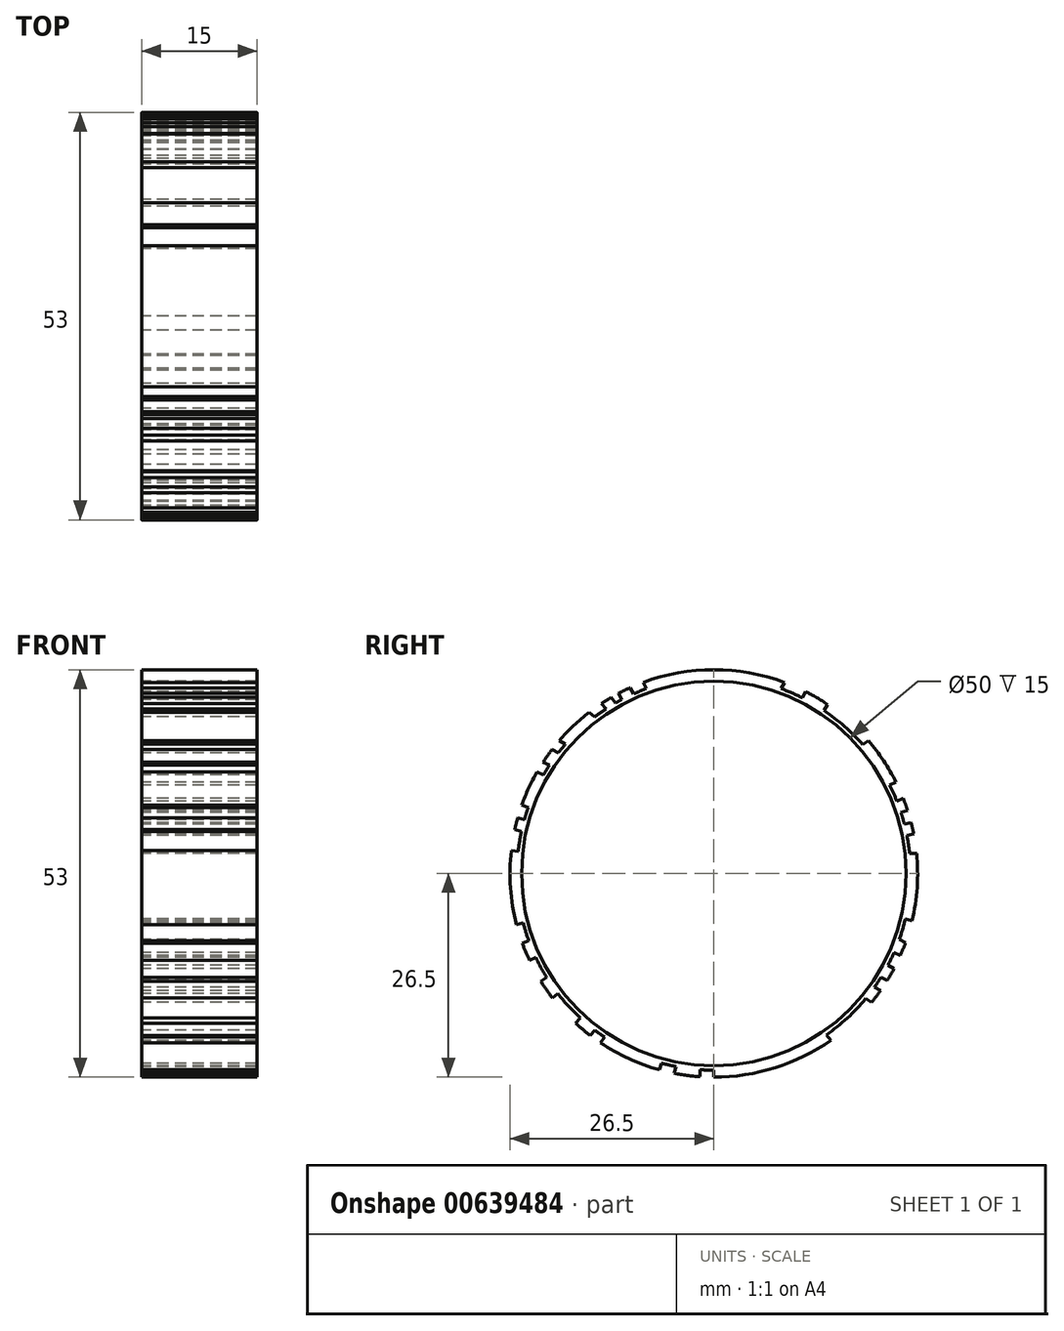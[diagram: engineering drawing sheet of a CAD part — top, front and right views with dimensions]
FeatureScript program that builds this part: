
annotation { "Feature Type Name" : "Feature", "Feature Type Description" : "" }
export const myFeature = defineFeature(function(context is Context, id is Id, definition is map)
    precondition{}
    {
        {
            var Q0;
            Q0=qCreatedBy(makeId("Right.planeOp"),FACE);
            var sketch = newSketch(context, id + "F0", { "sketchPlane" : qUnion([Q0])});
            skCircle(sketch, "E0", {"center": v(0, 0) * mm, "radius": 25 * mm});
            skSolve(sketch);
        }
        {
            var Q0;
            Q0=makeQuery(id+"F0.imprint","IMPRINT",FACE,{"disambiguationData":[TD([[makeQuery(id+"F0.imprint","IMPRINT",EDGE,{"derivedFrom":sQuery(id+"F0.wireOp",EDGE,"E0")}),1.0]])]});
            extrude(context, id + "F1", {"entities" : qUnion([Q0]), "depth" : 15 * mm, "offsetDistance" : 25 * mm});
        }
        {
            var Q0;
            Q0=qCreatedBy(makeId("Right.planeOp"),FACE);
            var sketch = newSketch(context, id + "F2", { "sketchPlane" : qUnion([Q0])});
            skArc(sketch, "E1", {"start": v(9.17, 24.86) * mm, "mid": v(0, 26.5) * mm, "end": v(-9.17, 24.86) * mm});
            skArc(sketch, "E2.0", {"start": v(-15.02, 19.99) * mm, "mid": v(13.77, -20.87) * mm, "end": v(-12.47, 21.67) * mm});
            skLineSegment(sketch, "E3", {"start": v(8.77, 24.05) * mm, "end": v(9.17, 24.86) * mm});
            skLineSegment(sketch, "E4.MirrorCS", {"start": v(-8.77, 24.05) * mm, "end": v(-9.17, 24.86) * mm});
            skLineSegment(sketch, "E5.0", {"start": v(11.2, 22.2) * mm, "end": v(11.26, 22.32) * mm});
            skLineSegment(sketch, "E6", {"start": v(14.32, 21.21) * mm, "end": v(14.77, 22) * mm});
            skLineSegment(sketch, "E7", {"start": v(11.86, 23.55) * mm, "end": v(11.92, 23.67) * mm});
            skLineSegment(sketch, "E8", {"start": v(-10.45, 23.36) * mm, "end": v(-10.88, 24.16) * mm});
            skLineSegment(sketch, "E9", {"start": v(-11.96, 22.63) * mm, "end": v(-12.4, 23.42) * mm});
            skArc(sketch, "E10.trimOffspring", {"start": v(-10.88, 24.16) * mm, "mid": v(-11.65, 23.8) * mm, "end": v(-12.4, 23.42) * mm});
            skLineSegment(sketch, "E11", {"start": v(19.35, 16.75) * mm, "end": v(20.1, 17.27) * mm});
            skLineSegment(sketch, "E12", {"start": v(22.88, 11.47) * mm, "end": v(23.7, 11.85) * mm});
            skLineSegment(sketch, "E13", {"start": v(23.8, 9.42) * mm, "end": v(24.64, 9.76) * mm});
            skLineSegment(sketch, "E14", {"start": v(24.33, 7.95) * mm, "end": v(25.2, 8.22) * mm});
            skArc(sketch, "E15.trimOffspring", {"start": v(23.7, 11.85) * mm, "mid": v(22.07, 14.67) * mm, "end": v(20.1, 17.27) * mm});
            skArc(sketch, "E16.trimOffspring", {"start": v(14.77, 22) * mm, "mid": v(13.37, 22.88) * mm, "end": v(11.92, 23.67) * mm});
            skLineSegment(sketch, "E17", {"start": v(24.78, 6.4) * mm, "end": v(25.66, 6.62) * mm});
            skLineSegment(sketch, "E18", {"start": v(25.1, 4.95) * mm, "end": v(26, 5.12) * mm});
            skArc(sketch, "E19.trimOffspring", {"start": v(25.2, 8.22) * mm, "mid": v(24.93, 9) * mm, "end": v(24.64, 9.76) * mm});
            skLineSegment(sketch, "E20", {"start": v(25.46, 2.62) * mm, "end": v(26.37, 2.62) * mm});
            skLineSegment(sketch, "E21", {"start": v(24.9, -5.88) * mm, "end": v(25.77, -6.18) * mm});
            skArc(sketch, "E22.trimOffspring", {"start": v(26, 5.12) * mm, "mid": v(25.84, 5.88) * mm, "end": v(25.66, 6.62) * mm});
            skLineSegment(sketch, "E23", {"start": v(-12.8, 22.16) * mm, "end": v(-13.32, 22.9) * mm});
            skLineSegment(sketch, "E24", {"start": v(-14.02, 21.41) * mm, "end": v(-14.6, 22.11) * mm});
            skArc(sketch, "E25.trimOffspring", {"start": v(-13.32, 22.9) * mm, "mid": v(-13.97, 22.52) * mm, "end": v(-14.6, 22.11) * mm});
            skLineSegment(sketch, "E26", {"start": v(-15.49, 20.38) * mm, "end": v(-16.2, 20.97) * mm});
            skLineSegment(sketch, "E27", {"start": v(-19.3, 16.8) * mm, "end": v(-20.08, 17.29) * mm});
            skArc(sketch, "E28.trimOffspring", {"start": v(-16.2, 20.97) * mm, "mid": v(-18.24, 19.23) * mm, "end": v(-20.08, 17.29) * mm});
            skLineSegment(sketch, "E29", {"start": v(-12.52, 21.75) * mm, "end": v(-12.47, 21.67) * mm});
            skLineSegment(sketch, "E30", {"start": v(24.12, -8.56) * mm, "end": v(24.93, -9) * mm});
            skLineSegment(sketch, "E31", {"start": v(23.44, -10.28) * mm, "end": v(24.27, -10.65) * mm});
            skArc(sketch, "E32.trimOffspring", {"start": v(25.77, -6.18) * mm, "mid": v(26.44, -1.8) * mm, "end": v(26.37, 2.62) * mm});
            skLineSegment(sketch, "E33", {"start": v(22.64, -11.94) * mm, "end": v(23.43, -12.38) * mm});
            skLineSegment(sketch, "E34", {"start": v(21.75, -13.5) * mm, "end": v(22.56, -13.9) * mm});
            skArc(sketch, "E35.trimOffspring", {"start": v(24.27, -10.65) * mm, "mid": v(24.61, -9.83) * mm, "end": v(24.93, -9) * mm});
            skLineSegment(sketch, "E36", {"start": v(20.9, -14.77) * mm, "end": v(21.67, -15.25) * mm});
            skLineSegment(sketch, "E37", {"start": v(19.75, -16.27) * mm, "end": v(20.52, -16.77) * mm});
            skArc(sketch, "E38.trimOffspring", {"start": v(22.56, -13.9) * mm, "mid": v(23, -13.15) * mm, "end": v(23.43, -12.38) * mm});
            skLineSegment(sketch, "E39", {"start": v(14.63, -21) * mm, "end": v(15.22, -21.7) * mm});
            skLineSegment(sketch, "E40", {"start": v(0, -25.6) * mm, "end": v(0, -26.5) * mm});
            skArc(sketch, "E41.trimOffspring", {"start": v(20.52, -16.77) * mm, "mid": v(21.1, -16.02) * mm, "end": v(21.67, -15.25) * mm});
            skLineSegment(sketch, "E42", {"start": v(-1.81, -25.53) * mm, "end": v(-1.81, -26.44) * mm});
            skLineSegment(sketch, "E43", {"start": v(-4.92, -25.12) * mm, "end": v(-5.14, -26) * mm});
            skArc(sketch, "E44.trimOffspring", {"start": v(0, -26.5) * mm, "mid": v(7.98, -25.27) * mm, "end": v(15.22, -21.7) * mm});
            skLineSegment(sketch, "E45", {"start": v(-20.23, 15.68) * mm, "end": v(-21.01, 16.14) * mm});
            skLineSegment(sketch, "E46", {"start": v(-21.37, 14.08) * mm, "end": v(-22.2, 14.46) * mm});
            skArc(sketch, "E47.trimOffspring", {"start": v(-21.01, 16.14) * mm, "mid": v(-21.63, 15.31) * mm, "end": v(-22.2, 14.46) * mm});
            skLineSegment(sketch, "E48", {"start": v(-22.15, 12.81) * mm, "end": v(-22.98, 13.2) * mm});
            skLineSegment(sketch, "E49", {"start": v(-24.1, 8.6) * mm, "end": v(-24.96, 8.91) * mm});
            skArc(sketch, "E50.trimOffspring", {"start": v(-22.98, 13.2) * mm, "mid": v(-24.06, 11.1) * mm, "end": v(-24.96, 8.91) * mm});
            skLineSegment(sketch, "E51", {"start": v(-6.8, -24.68) * mm, "end": v(-7.05, -25.55) * mm});
            skLineSegment(sketch, "E52", {"start": v(-14.2, -21.3) * mm, "end": v(-14.76, -22) * mm});
            skArc(sketch, "E53.trimOffspring", {"start": v(-5.14, -26) * mm, "mid": v(-3.49, -26.27) * mm, "end": v(-1.81, -26.44) * mm});
            skLineSegment(sketch, "E54", {"start": v(-24.62, 7) * mm, "end": v(-25.49, 7.26) * mm});
            skLineSegment(sketch, "E55", {"start": v(-25, 5.46) * mm, "end": v(-25.88, 5.7) * mm});
            skArc(sketch, "E56.trimOffspring", {"start": v(-25.49, 7.26) * mm, "mid": v(-25.7, 6.48) * mm, "end": v(-25.88, 5.7) * mm});
            skLineSegment(sketch, "E57", {"start": v(-25.43, 2.89) * mm, "end": v(-26.33, 2.98) * mm});
            skLineSegment(sketch, "E58", {"start": v(-24.77, -6.44) * mm, "end": v(-25.65, -6.64) * mm});
            skArc(sketch, "E59.trimOffspring", {"start": v(-26.33, 2.98) * mm, "mid": v(-26.43, -1.86) * mm, "end": v(-25.65, -6.64) * mm});
            skLineSegment(sketch, "E60", {"start": v(-24.06, -8.73) * mm, "end": v(-24.9, -9.08) * mm});
            skLineSegment(sketch, "E61", {"start": v(-23.14, -10.93) * mm, "end": v(-23.98, -11.28) * mm});
            skArc(sketch, "E62.trimOffspring", {"start": v(-24.9, -9.08) * mm, "mid": v(-24.46, -10.19) * mm, "end": v(-23.98, -11.28) * mm});
            skLineSegment(sketch, "E63", {"start": v(-15.46, -20.4) * mm, "end": v(-16.1, -21.05) * mm});
            skLineSegment(sketch, "E64", {"start": v(-17.36, -18.8) * mm, "end": v(-17.97, -19.48) * mm});
            skArc(sketch, "E65.trimOffspring", {"start": v(-14.76, -22) * mm, "mid": v(-11.05, -24.09) * mm, "end": v(-7.05, -25.55) * mm});
            skLineSegment(sketch, "E66", {"start": v(-21.71, -13.55) * mm, "end": v(-22.47, -14.05) * mm});
            skLineSegment(sketch, "E67", {"start": v(-20.27, -15.63) * mm, "end": v(-21, -16.16) * mm});
            skArc(sketch, "E68.trimOffspring", {"start": v(-22.47, -14.05) * mm, "mid": v(-21.76, -15.12) * mm, "end": v(-21, -16.16) * mm});
            skArc(sketch, "E69.trimOffspring", {"start": v(-17.97, -19.48) * mm, "mid": v(-17.05, -20.29) * mm, "end": v(-16.1, -21.05) * mm});
            skArc(sketch, "E70", {"start": v(-8.77, 24.05) * mm, "mid": v(-9.61, 23.72) * mm, "end": v(-10.45, 23.36) * mm});
            skLineSegment(sketch, "E71.trimOffspring", {"start": v(11.52, 22.85) * mm, "end": v(11.86, 23.55) * mm});
            skArc(sketch, "E72.trimOffspring", {"start": v(11.52, 22.85) * mm, "mid": v(10.16, 23.49) * mm, "end": v(8.77, 24.05) * mm});
            skArc(sketch, "E73.trimOffspring", {"start": v(19.35, 16.75) * mm, "mid": v(16.98, 19.15) * mm, "end": v(14.32, 21.21) * mm});
            skArc(sketch, "E74.trimOffspring", {"start": v(-11.96, 22.63) * mm, "mid": v(-12.38, 22.4) * mm, "end": v(-12.8, 22.16) * mm});
            skArc(sketch, "E75.trimOffspring", {"start": v(-14.02, 21.41) * mm, "mid": v(-14.76, 20.9) * mm, "end": v(-15.49, 20.38) * mm});
            skArc(sketch, "E76.trimOffspring", {"start": v(-19.3, 16.8) * mm, "mid": v(-19.78, 16.25) * mm, "end": v(-20.23, 15.68) * mm});
            skArc(sketch, "E77.trimOffspring", {"start": v(-21.37, 14.08) * mm, "mid": v(-21.77, 13.45) * mm, "end": v(-22.15, 12.81) * mm});
            skArc(sketch, "E78.trimOffspring", {"start": v(-24.1, 8.6) * mm, "mid": v(-24.37, 7.8) * mm, "end": v(-24.62, 7) * mm});
            skArc(sketch, "E79.trimOffspring", {"start": v(-25, 5.46) * mm, "mid": v(-25.25, 4.18) * mm, "end": v(-25.43, 2.89) * mm});
            skArc(sketch, "E80.trimOffspring", {"start": v(-24.77, -6.44) * mm, "mid": v(-24.44, -7.6) * mm, "end": v(-24.06, -8.73) * mm});
            skArc(sketch, "E81.trimOffspring", {"start": v(-23.14, -10.93) * mm, "mid": v(-22.47, -12.26) * mm, "end": v(-21.71, -13.55) * mm});
            skArc(sketch, "E82.trimOffspring", {"start": v(-20.27, -15.63) * mm, "mid": v(-18.88, -17.28) * mm, "end": v(-17.36, -18.8) * mm});
            skArc(sketch, "E83.trimOffspring", {"start": v(-15.46, -20.4) * mm, "mid": v(-14.84, -20.85) * mm, "end": v(-14.2, -21.3) * mm});
            skArc(sketch, "E84.trimOffspring", {"start": v(-6.8, -24.68) * mm, "mid": v(-5.86, -24.91) * mm, "end": v(-4.92, -25.12) * mm});
            skArc(sketch, "E85.trimOffspring", {"start": v(-1.81, -25.53) * mm, "mid": v(-0.9, -25.58) * mm, "end": v(0, -25.6) * mm});
            skPoint(sketch, "E86.orphan", {"position": v(0, -25) * mm});
            skArc(sketch, "E87.trimOffspring", {"start": v(14.63, -21) * mm, "mid": v(17.36, -18.81) * mm, "end": v(19.75, -16.27) * mm});
            skArc(sketch, "E88.trimOffspring", {"start": v(20.9, -14.77) * mm, "mid": v(21.33, -14.14) * mm, "end": v(21.75, -13.5) * mm});
            skArc(sketch, "E89.trimOffspring", {"start": v(22.64, -11.94) * mm, "mid": v(23.05, -11.12) * mm, "end": v(23.44, -10.28) * mm});
            skArc(sketch, "E90.trimOffspring", {"start": v(24.12, -8.56) * mm, "mid": v(24.55, -7.24) * mm, "end": v(24.9, -5.88) * mm});
            skArc(sketch, "E91.trimOffspring", {"start": v(25.46, 2.62) * mm, "mid": v(25.31, 3.79) * mm, "end": v(25.1, 4.95) * mm});
            skArc(sketch, "E92.trimOffspring", {"start": v(24.78, 6.4) * mm, "mid": v(24.57, 7.18) * mm, "end": v(24.33, 7.95) * mm});
            skArc(sketch, "E93.trimOffspring", {"start": v(23.8, 9.42) * mm, "mid": v(23.36, 10.46) * mm, "end": v(22.88, 11.47) * mm});
            skCircle(sketch, "E94.0.0", {"center": v(0, 0) * mm, "radius": 25 * mm});
            skSolve(sketch);
        }
        {
            var Q0;
            Q0=makeQuery(id+"F2.imprint","IMPRINT",FACE,{"disambiguationData":[TD([[makeQuery(id+"F2.imprint","IMPRINT",EDGE,{"derivedFrom":sQuery(id+"F2.wireOp",EDGE,"E1")}),1.0]])]});
            extrude(context, id + "F3", {"entities" : qUnion([Q0]), "operationType" : NewBodyOperationType.ADD, "depth" : 15 * mm, "offsetDistance" : 25 * mm});
        }
        {
            var Q0;
            {var subQ3=sQuery(id+"F2.wireOp",EDGE,"E94.0.0");Q0=makeQuery(id+"F2.imprint","IMPRINT",FACE,{"disambiguationData":[TD([[makeQuery(id+"F2.imprint","IMPRINT",EDGE,{"derivedFrom":subQ3}),1.0]])]});}
            extrude(context, id + "F4", {"entities" : qUnion([Q0]), "operationType" : NewBodyOperationType.REMOVE, "depth" : 25 * mm, "offsetDistance" : 25 * mm});
        }
    });
